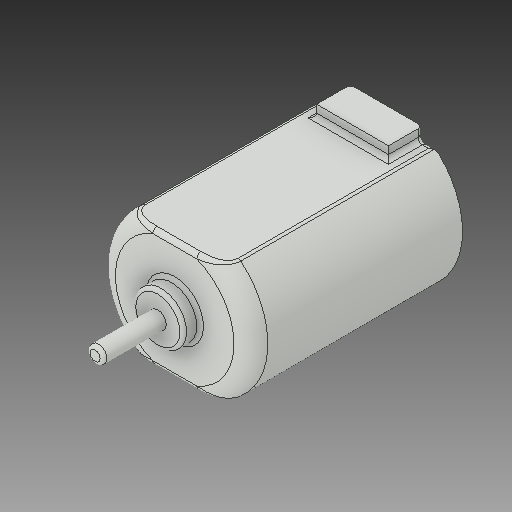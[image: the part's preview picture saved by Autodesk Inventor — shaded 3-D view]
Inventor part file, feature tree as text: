
AUTODESK INVENTOR PART (.ipt)
format: ipt  version: 2019.1 (Build 231200000, 200)  size: 228,864 bytes
history: mixed  units: in
note: dims shown in document units (in); Inventor stores cm internally (conversion verified against a paired STEP export)
features: fillet x1, imported_body x1
ambient origin geometry x8: Origin, YZ Plane, XZ Plane, XY Plane, X Axis, Y Axis, Z Axis, Center Point
bodies: Solid1 (imported_parasolid)
feature tree (2):
  fillet  "Fillet5"  [1 undecoded]
  imported_body  NMx_Import_Brep_tag  [imported B-rep: ~10 faces, bbox_mm=[9.088514, 13.0, 2.3]]
note: 1 required parameter value undecoded (feature->parameter linkage not recoverable at this tier; creation-order binding heuristic only, values carry confidence <= 0.55)
